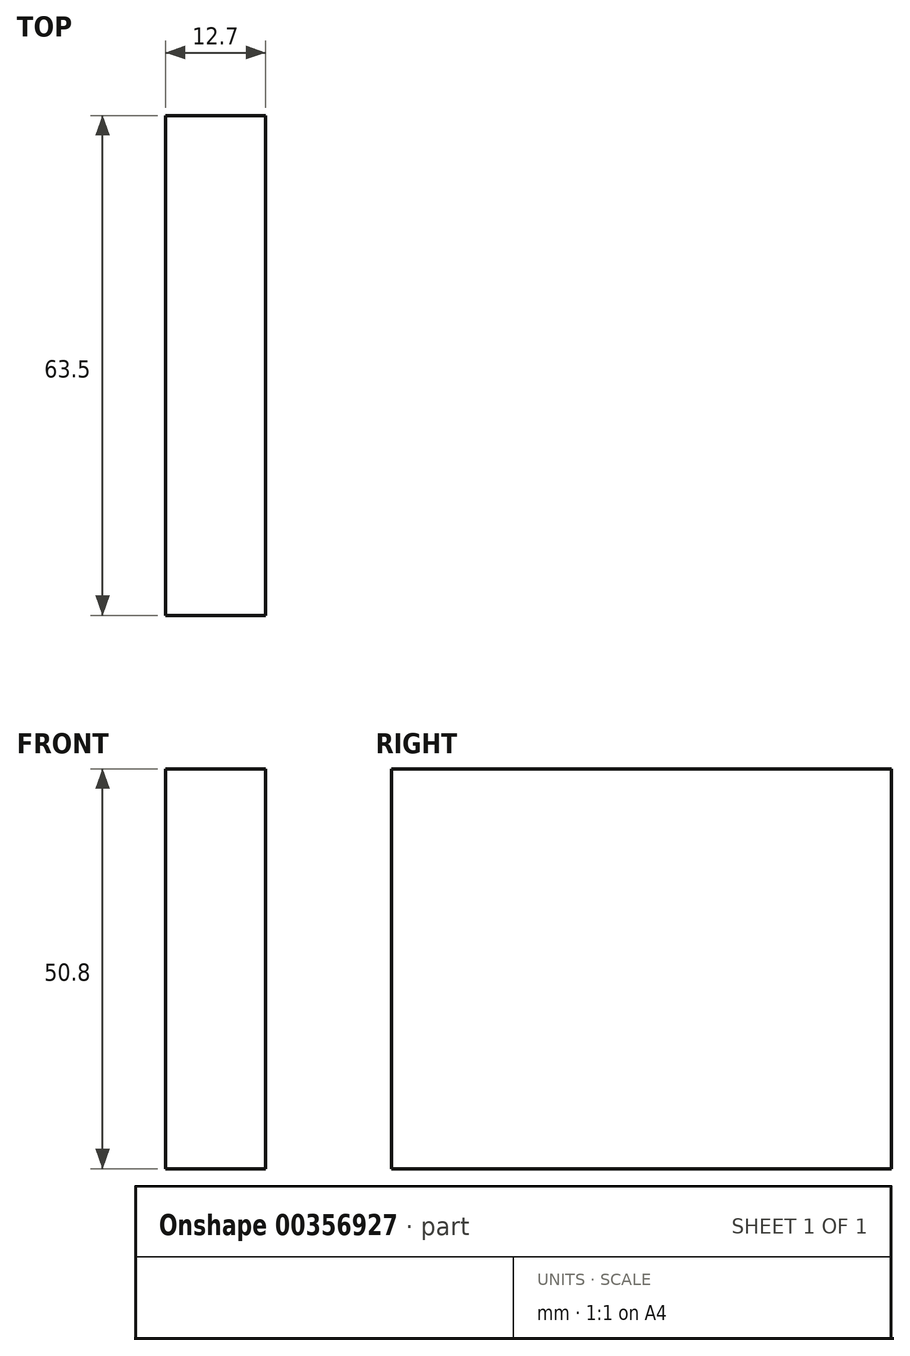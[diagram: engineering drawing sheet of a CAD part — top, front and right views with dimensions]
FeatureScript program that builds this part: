
annotation { "Feature Type Name" : "Feature", "Feature Type Description" : "" }
export const myFeature = defineFeature(function(context is Context, id is Id, definition is map)
    precondition{}
    {
        {
            var Q0;
            Q0=qCreatedBy(makeId("Front.planeOp"),FACE);
            var sketch = newSketch(context, id + "F0", { "sketchPlane" : qUnion([Q0])});
            skLineSegment(sketch, "E0.bottom", {"start": v(0, 0) * mm, "end": v(12.7, 0) * mm});
            skLineSegment(sketch, "E0.top", {"start": v(0, -50.8) * mm, "end": v(12.7, -50.8) * mm});
            skLineSegment(sketch, "E0.left", {"start": v(0, 0) * mm, "end": v(0, -50.8) * mm});
            skLineSegment(sketch, "E0.right", {"start": v(12.7, 0) * mm, "end": v(12.7, -50.8) * mm});
            skSolve(sketch);
        }
        {
            var Q0;
            Q0=makeQuery(id+"F0.imprint","IMPRINT",FACE,{"disambiguationData":[TD([[makeQuery(id+"F0.imprint","IMPRINT",EDGE,{"derivedFrom":sQuery(id+"F0.wireOp",EDGE,"E0.bottom")}),-1.0]])]});
            extrude(context, id + "F1", {"entities" : qUnion([Q0]), "depth" : 63.5 * mm});
        }
    });
